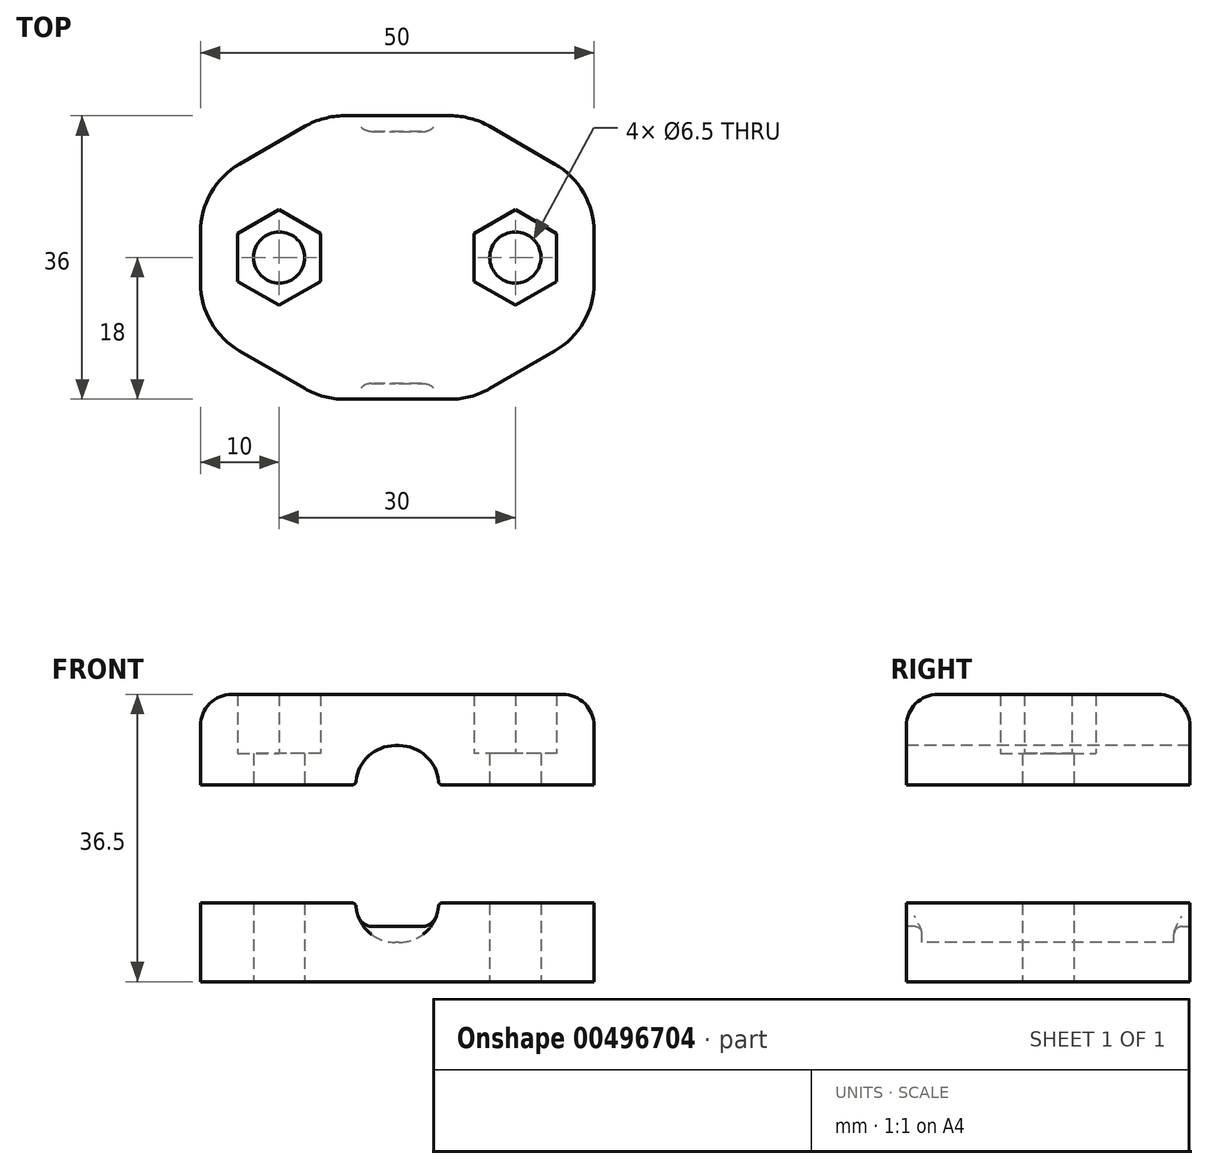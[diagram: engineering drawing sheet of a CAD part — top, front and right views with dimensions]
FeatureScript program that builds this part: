
annotation { "Feature Type Name" : "Feature", "Feature Type Description" : "" }
export const myFeature = defineFeature(function(context is Context, id is Id, definition is map)
    precondition{}
    {
        {
            var Q0;
            Q0=qCreatedBy(makeId("Top.planeOp"),FACE);
            var sketch = newSketch(context, id + "F0", { "sketchPlane" : qUnion([Q0])});
            skLineSegment(sketch, "E0.bottom", {"start": v(9.41, 18) * mm, "end": v(-9.41, 18) * mm});
            skLineSegment(sketch, "E0.top", {"start": v(9.41, -18) * mm, "end": v(-9.41, -18) * mm});
            skLineSegment(sketch, "E0.left", {"start": v(25, 9) * mm, "end": v(25, -18) * mm});
            skLineSegment(sketch, "E0.right", {"start": v(-25, 9) * mm, "end": v(-25, -9) * mm});
            skPoint(sketch, "E0.middle", {"position": v(0, 0) * mm});
            skLineSegment(sketch, "E1.0", {"start": v(9.41, 18) * mm, "end": v(25, 9) * mm});
            skLineSegment(sketch, "E1.1", {"start": v(25, 9) * mm, "end": v(25, -9) * mm});
            skLineSegment(sketch, "E1.2", {"start": v(25, -9) * mm, "end": v(9.41, -18) * mm});
            skLineSegment(sketch, "E1.3", {"start": v(-9.41, -18) * mm, "end": v(-25, -9) * mm});
            skLineSegment(sketch, "E1.4", {"start": v(-25, -9) * mm, "end": v(-25, 9) * mm});
            skLineSegment(sketch, "E1.5", {"start": v(-25, 9) * mm, "end": v(-9.41, 18) * mm});
            skPoint(sketch, "E2.orphan", {"position": v(-25, 18) * mm});
            skPoint(sketch, "E3.orphan", {"position": v(-25, -18) * mm});
            skPoint(sketch, "E4.orphan", {"position": v(25, 18) * mm});
            skSolve(sketch);
        }
        {
            var Q0;
            Q0=makeQuery(id+"F0.imprint","IMPRINT",FACE,{"disambiguationData":[TD([[makeQuery(id+"F0.imprint","IMPRINT",EDGE,{"derivedFrom":sQuery(id+"F0.wireOp",EDGE,"E0.bottom")}),1.0]])]});
            var sketch = newSketch(context, id + "F1", { "sketchPlane" : qUnion([Q0])});
            skLineSegment(sketch, "E5.bottom", {"start": v(5.25, 16) * mm, "end": v(-5.25, 16) * mm});
            skLineSegment(sketch, "E5.top", {"start": v(5.25, -16) * mm, "end": v(-5.25, -16) * mm});
            skLineSegment(sketch, "E5.left", {"start": v(5.25, 16) * mm, "end": v(5.25, -16) * mm});
            skLineSegment(sketch, "E5.right", {"start": v(-5.25, 16) * mm, "end": v(-5.25, -16) * mm});
            skPoint(sketch, "E5.middle", {"position": v(0, 0) * mm});
            skSolve(sketch);
        }
        {
            var Q0;
            Q0=qCreatedBy(makeId("Top.planeOp"),FACE);
            var sketch = newSketch(context, id + "F2", { "sketchPlane" : qUnion([Q0])});
            skLineSegment(sketch, "E6.bottom", {"start": v(5.25, 20) * mm, "end": v(-5.25, 20) * mm});
            skLineSegment(sketch, "E6.top", {"start": v(5.25, -20) * mm, "end": v(-5.25, -20) * mm});
            skLineSegment(sketch, "E6.left", {"start": v(5.25, 20) * mm, "end": v(5.25, -20) * mm});
            skLineSegment(sketch, "E6.right", {"start": v(-5.25, 20) * mm, "end": v(-5.25, -20) * mm});
            skPoint(sketch, "E6.middle", {"position": v(0, 0) * mm});
            skSolve(sketch);
        }
        {
            var Q0;
            Q0=makeQuery(id+"F0.imprint","IMPRINT",FACE,{"disambiguationData":[TD([[makeQuery(id+"F0.imprint","IMPRINT",EDGE,{"derivedFrom":sQuery(id+"F0.wireOp",EDGE,"E0.bottom")}),1.0]])]});
            var sketch = newSketch(context, id + "F3", { "sketchPlane" : qUnion([Q0])});
            skCircle(sketch, "E7", {"center": v(-15, 0) * mm, "radius": 3.25 * mm});
            skLineSegment(sketch, "E8", {"start": v(-15, 0) * mm, "end": v(15, 0) * mm, "construction": true});
            skCircle(sketch, "E9", {"center": v(15, 0) * mm, "radius": 3.25 * mm});
            skSolve(sketch);
        }
        {
            var Q0;
            Q0 = qSketchRegion(id + "F0", true);
            extrude(context, id + "F4", {"entities" : qUnion([Q0]), "depth" : 10 * mm});
        }
        {
            var Q0;
            Q0 = qSketchRegion(id + "F0", true);
            extrude(context, id + "F5", {"entities" : qUnion([Q0]), "depth" : 36.5 * mm, "hasSecondDirection" : true, "secondDirectionOppositeDirection" : false, "secondDirectionDepth" : 25 * mm, "offsetDistance" : 25 * mm});
        }
        {
            var Q0;
            Q0 = qSketchRegion(id + "F3", true);
            extrude(context, id + "F6", {"entities" : qUnion([Q0]), "operationType" : NewBodyOperationType.REMOVE, "endBound" : BoundingType.THROUGH_ALL, "depth" : 25 * mm});
        }
        {
            var Q0;
            Q0 = qSketchRegion(id + "F1", true);
            extrude(context, id + "F7", {"entities" : qUnion([Q0]), "operationType" : NewBodyOperationType.REMOVE, "depth" : 30 * mm, "hasSecondDirection" : true, "secondDirectionOppositeDirection" : false, "secondDirectionDepth" : 5 * mm});
        }
        {
            var Q0;
            Q0 = qSketchRegion(id + "F2", true);
            extrude(context, id + "F8", {"entities" : qUnion([Q0]), "operationType" : NewBodyOperationType.REMOVE, "depth" : 30 * mm, "hasSecondDirection" : true, "secondDirectionOppositeDirection" : false, "secondDirectionDepth" : 7 * mm, "offsetDistance" : 25 * mm});
        }
        {
            var Q0;
            Q0=makeQuery(id+"F3.imprint","IMPRINT",FACE,{"disambiguationData":[TD([[makeQuery(id+"F3.imprint","IMPRINT",EDGE,{"derivedFrom":sQuery(id+"F3.wireOp",EDGE,"E7")}),1.0]])]});
            var sketch = newSketch(context, id + "F9", { "sketchPlane" : qUnion([Q0])});
            skLineSegment(sketch, "E10", {"start": v(0, 0) * mm, "end": v(-15, 0) * mm});
            skLineSegment(sketch, "E11", {"start": v(-15, 0) * mm, "end": v(15, 0) * mm});
            skPoint(sketch, "E12.0.midPoint", {"position": v(-20, 0) * mm});
            skPoint(sketch, "E13.0.midPoint", {"position": v(20, 0) * mm});
            skCircle(sketch, "E14.cCircle", {"center": v(-15, 0) * mm, "radius": 5.25 * mm, "construction": true});
            skLineSegment(sketch, "E14.0", {"start": v(-20.25, -3.03) * mm, "end": v(-20.25, 3.03) * mm});
            skLineSegment(sketch, "E14.1", {"start": v(-20.25, 3.03) * mm, "end": v(-15, 6.06) * mm});
            skLineSegment(sketch, "E14.2", {"start": v(-15, 6.06) * mm, "end": v(-9.75, 3.03) * mm});
            skLineSegment(sketch, "E14.3", {"start": v(-9.75, 3.03) * mm, "end": v(-9.75, -3.03) * mm});
            skLineSegment(sketch, "E14.4", {"start": v(-9.75, -3.03) * mm, "end": v(-15, -6.06) * mm});
            skLineSegment(sketch, "E14.5", {"start": v(-15, -6.06) * mm, "end": v(-20.25, -3.03) * mm});
            skPoint(sketch, "E14.0.midPoint", {"position": v(-20.25, 0) * mm});
            skCircle(sketch, "E15.cCircle", {"center": v(15, 0) * mm, "radius": 5.25 * mm, "construction": true});
            skLineSegment(sketch, "E15.0", {"start": v(20.25, 3.03) * mm, "end": v(20.25, -3.03) * mm});
            skLineSegment(sketch, "E15.1", {"start": v(20.25, -3.03) * mm, "end": v(15, -6.06) * mm});
            skLineSegment(sketch, "E15.2", {"start": v(15, -6.06) * mm, "end": v(9.75, -3.03) * mm});
            skLineSegment(sketch, "E15.3", {"start": v(9.75, -3.03) * mm, "end": v(9.75, 3.03) * mm});
            skLineSegment(sketch, "E15.4", {"start": v(9.75, 3.03) * mm, "end": v(15, 6.06) * mm});
            skLineSegment(sketch, "E15.5", {"start": v(15, 6.06) * mm, "end": v(20.25, 3.03) * mm});
            skPoint(sketch, "E15.0.midPoint", {"position": v(20.25, 0) * mm});
            skSolve(sketch);
        }
        {
            var Q0;
            Q0 = qSketchRegion(id + "F9", true);
            extrude(context, id + "F10", {"entities" : qUnion([Q0]), "operationType" : NewBodyOperationType.REMOVE, "depth" : 40 * mm, "hasSecondDirection" : true, "secondDirectionOppositeDirection" : false, "secondDirectionDepth" : 29 * mm, "offsetDistance" : 25 * mm});
        }
        {
            var Q0;
            Q0=makeQuery(id+"F7.boolean.opBoolean","COPY",EDGE,{"derivedFrom":makeQuery(id+"F7.opExtrude","CAP_EDGE",EDGE,{"disambiguationData":[OSD([sQuery(id+"F1.wireOp",EDGE,"E5.left")])],"isStart":true})});
            var Q1;
            Q1=makeQuery(id+"F7.boolean.opBoolean","COPY",EDGE,{"derivedFrom":makeQuery(id+"F7.opExtrude","CAP_EDGE",EDGE,{"disambiguationData":[OSD([sQuery(id+"F1.wireOp",EDGE,"E5.right")])],"isStart":true})});
            var Q2;
            Q2=makeQuery(id+"F7.boolean.opBoolean","COPY",EDGE,{"derivedFrom":makeQuery(id+"F7.opExtrude","CAP_EDGE",EDGE,{"disambiguationData":[OSD([sQuery(id+"F1.wireOp",EDGE,"E5.left")])],"isStart":false})});
            var Q3;
            Q3=makeQuery(id+"F7.boolean.opBoolean","COPY",EDGE,{"derivedFrom":makeQuery(id+"F7.opExtrude","CAP_EDGE",EDGE,{"disambiguationData":[OSD([sQuery(id+"F1.wireOp",EDGE,"E5.right")])],"isStart":false})});
            fillet(context, id + "F11", {"entities" : qUnion([Q0, Q1, Q2, Q3]), "radius" : 5 * mm, "tangentPropagation" : true, "allowEdgeOverflow" : false});
        }
        {
            var Q0;
            {var subQ0=sQuery(id+"F0.wireOp",EDGE,"E0.bottom");var subQ6=sQuery(id+"F1.wireOp",EDGE,"E5.right");var subQ10=sQuery(id+"F2.wireOp",EDGE,"E6.left");var subQ12=sQuery(id+"F2.wireOp",EDGE,"E6.right");Q0=makeQuery(id+"F11.opFillet","BLEND_EDGE",EDGE,{"blendedFrom":[makeQuery(id+"F7.boolean.opBoolean","COPY",EDGE,{"derivedFrom":makeQuery(id+"F7.opExtrude","CAP_EDGE",EDGE,{"disambiguationData":[OSD([subQ6])],"isStart":true})}),makeQuery(id+"F8.boolean.opBoolean","COPY",FACE,{"disambiguationData":[TD([makeQuery(id+"F4.opExtrude","SWEPT_FACE",FACE,{"disambiguationData":[OSD([subQ0])]})])],"derivedFrom":makeQuery(id+"F8.opExtrude","CAP_FACE",FACE,{"disambiguationData":[OSD([sQuery(id+"F2.wireOp",EDGE,"E6.bottom"),sQuery(id+"F2.wireOp",EDGE,"E6.top"),subQ10,subQ12])],"isStart":true})})],"blendedInto":[makeQuery(id+"F8.boolean.opBoolean","COPY",FACE,{"disambiguationData":[TD([makeQuery(id+"F4.opExtrude","SWEPT_FACE",FACE,{"disambiguationData":[OSD([subQ0])]})])],"derivedFrom":makeQuery(id+"F8.opExtrude","CAP_FACE",FACE,{"disambiguationData":[OSD([sQuery(id+"F2.wireOp",EDGE,"E6.bottom"),sQuery(id+"F2.wireOp",EDGE,"E6.top"),subQ10,subQ12])],"isStart":true})})]});}
            var Q1;
            {var subQ0=sQuery(id+"F0.wireOp",EDGE,"E0.bottom");var subQ7=sQuery(id+"F1.wireOp",EDGE,"E5.left");var subQ10=sQuery(id+"F2.wireOp",EDGE,"E6.left");var subQ12=sQuery(id+"F2.wireOp",EDGE,"E6.right");Q1=makeQuery(id+"F11.opFillet","BLEND_EDGE",EDGE,{"blendedFrom":[makeQuery(id+"F7.boolean.opBoolean","COPY",EDGE,{"derivedFrom":makeQuery(id+"F7.opExtrude","CAP_EDGE",EDGE,{"disambiguationData":[OSD([subQ7])],"isStart":true})}),makeQuery(id+"F8.boolean.opBoolean","COPY",FACE,{"disambiguationData":[TD([makeQuery(id+"F4.opExtrude","SWEPT_FACE",FACE,{"disambiguationData":[OSD([subQ0])]})])],"derivedFrom":makeQuery(id+"F8.opExtrude","CAP_FACE",FACE,{"disambiguationData":[OSD([sQuery(id+"F2.wireOp",EDGE,"E6.bottom"),sQuery(id+"F2.wireOp",EDGE,"E6.top"),subQ10,subQ12])],"isStart":true})})],"blendedInto":[makeQuery(id+"F8.boolean.opBoolean","COPY",FACE,{"disambiguationData":[TD([makeQuery(id+"F4.opExtrude","SWEPT_FACE",FACE,{"disambiguationData":[OSD([subQ0])]})])],"derivedFrom":makeQuery(id+"F8.opExtrude","CAP_FACE",FACE,{"disambiguationData":[OSD([sQuery(id+"F2.wireOp",EDGE,"E6.bottom"),sQuery(id+"F2.wireOp",EDGE,"E6.top"),subQ10,subQ12])],"isStart":true})})]});}
            var Q2;
            {var subQ0=sQuery(id+"F0.wireOp",EDGE,"E0.top");var subQ6=sQuery(id+"F1.wireOp",EDGE,"E5.right");var subQ11=sQuery(id+"F2.wireOp",EDGE,"E6.left");var subQ12=sQuery(id+"F2.wireOp",EDGE,"E6.right");Q2=makeQuery(id+"F11.opFillet","BLEND_EDGE",EDGE,{"blendedFrom":[makeQuery(id+"F7.boolean.opBoolean","COPY",EDGE,{"derivedFrom":makeQuery(id+"F7.opExtrude","CAP_EDGE",EDGE,{"disambiguationData":[OSD([subQ6])],"isStart":true})}),makeQuery(id+"F8.boolean.opBoolean","COPY",FACE,{"disambiguationData":[TD([makeQuery(id+"F4.opExtrude","SWEPT_FACE",FACE,{"disambiguationData":[OSD([subQ0])]})])],"derivedFrom":makeQuery(id+"F8.opExtrude","CAP_FACE",FACE,{"disambiguationData":[OSD([sQuery(id+"F2.wireOp",EDGE,"E6.bottom"),sQuery(id+"F2.wireOp",EDGE,"E6.top"),subQ11,subQ12])],"isStart":true})})],"blendedInto":[makeQuery(id+"F8.boolean.opBoolean","COPY",FACE,{"disambiguationData":[TD([makeQuery(id+"F4.opExtrude","SWEPT_FACE",FACE,{"disambiguationData":[OSD([subQ0])]})])],"derivedFrom":makeQuery(id+"F8.opExtrude","CAP_FACE",FACE,{"disambiguationData":[OSD([sQuery(id+"F2.wireOp",EDGE,"E6.bottom"),sQuery(id+"F2.wireOp",EDGE,"E6.top"),subQ11,subQ12])],"isStart":true})})]});}
            var Q3;
            {var subQ0=sQuery(id+"F0.wireOp",EDGE,"E0.top");var subQ7=sQuery(id+"F1.wireOp",EDGE,"E5.left");var subQ11=sQuery(id+"F2.wireOp",EDGE,"E6.left");var subQ12=sQuery(id+"F2.wireOp",EDGE,"E6.right");Q3=makeQuery(id+"F11.opFillet","BLEND_EDGE",EDGE,{"blendedFrom":[makeQuery(id+"F7.boolean.opBoolean","COPY",EDGE,{"derivedFrom":makeQuery(id+"F7.opExtrude","CAP_EDGE",EDGE,{"disambiguationData":[OSD([subQ7])],"isStart":true})}),makeQuery(id+"F8.boolean.opBoolean","COPY",FACE,{"disambiguationData":[TD([makeQuery(id+"F4.opExtrude","SWEPT_FACE",FACE,{"disambiguationData":[OSD([subQ0])]})])],"derivedFrom":makeQuery(id+"F8.opExtrude","CAP_FACE",FACE,{"disambiguationData":[OSD([sQuery(id+"F2.wireOp",EDGE,"E6.bottom"),sQuery(id+"F2.wireOp",EDGE,"E6.top"),subQ11,subQ12])],"isStart":true})})],"blendedInto":[makeQuery(id+"F8.boolean.opBoolean","COPY",FACE,{"disambiguationData":[TD([makeQuery(id+"F4.opExtrude","SWEPT_FACE",FACE,{"disambiguationData":[OSD([subQ0])]})])],"derivedFrom":makeQuery(id+"F8.opExtrude","CAP_FACE",FACE,{"disambiguationData":[OSD([sQuery(id+"F2.wireOp",EDGE,"E6.bottom"),sQuery(id+"F2.wireOp",EDGE,"E6.top"),subQ11,subQ12])],"isStart":true})})]});}
            var Q4;
            {var subQ0=sQuery(id+"F0.wireOp",EDGE,"E0.bottom");var subQ6=sQuery(id+"F1.wireOp",EDGE,"E5.right");var subQ10=sQuery(id+"F2.wireOp",EDGE,"E6.right");var subQ12=sQuery(id+"F2.wireOp",EDGE,"E6.left");Q4=makeQuery(id+"F11.opFillet","BLEND_EDGE",EDGE,{"blendedFrom":[makeQuery(id+"F7.boolean.opBoolean","COPY",EDGE,{"derivedFrom":makeQuery(id+"F7.opExtrude","CAP_EDGE",EDGE,{"disambiguationData":[OSD([subQ6])],"isStart":false})}),makeQuery(id+"F8.boolean.opBoolean","COPY",FACE,{"disambiguationData":[TD([makeQuery(id+"F5.opExtrude","SWEPT_FACE",FACE,{"disambiguationData":[OSD([subQ0])]})])],"derivedFrom":makeQuery(id+"F8.opExtrude","CAP_FACE",FACE,{"disambiguationData":[OSD([sQuery(id+"F2.wireOp",EDGE,"E6.bottom"),sQuery(id+"F2.wireOp",EDGE,"E6.top"),subQ12,subQ10])],"isStart":false})})],"blendedInto":[makeQuery(id+"F8.boolean.opBoolean","COPY",FACE,{"disambiguationData":[TD([makeQuery(id+"F5.opExtrude","SWEPT_FACE",FACE,{"disambiguationData":[OSD([subQ0])]})])],"derivedFrom":makeQuery(id+"F8.opExtrude","CAP_FACE",FACE,{"disambiguationData":[OSD([sQuery(id+"F2.wireOp",EDGE,"E6.bottom"),sQuery(id+"F2.wireOp",EDGE,"E6.top"),subQ12,subQ10])],"isStart":false})})]});}
            var Q5;
            {var subQ0=sQuery(id+"F0.wireOp",EDGE,"E0.bottom");var subQ7=sQuery(id+"F1.wireOp",EDGE,"E5.left");var subQ10=sQuery(id+"F2.wireOp",EDGE,"E6.right");var subQ12=sQuery(id+"F2.wireOp",EDGE,"E6.left");Q5=makeQuery(id+"F11.opFillet","BLEND_EDGE",EDGE,{"blendedFrom":[makeQuery(id+"F7.boolean.opBoolean","COPY",EDGE,{"derivedFrom":makeQuery(id+"F7.opExtrude","CAP_EDGE",EDGE,{"disambiguationData":[OSD([subQ7])],"isStart":false})}),makeQuery(id+"F8.boolean.opBoolean","COPY",FACE,{"disambiguationData":[TD([makeQuery(id+"F5.opExtrude","SWEPT_FACE",FACE,{"disambiguationData":[OSD([subQ0])]})])],"derivedFrom":makeQuery(id+"F8.opExtrude","CAP_FACE",FACE,{"disambiguationData":[OSD([sQuery(id+"F2.wireOp",EDGE,"E6.bottom"),sQuery(id+"F2.wireOp",EDGE,"E6.top"),subQ12,subQ10])],"isStart":false})})],"blendedInto":[makeQuery(id+"F8.boolean.opBoolean","COPY",FACE,{"disambiguationData":[TD([makeQuery(id+"F5.opExtrude","SWEPT_FACE",FACE,{"disambiguationData":[OSD([subQ0])]})])],"derivedFrom":makeQuery(id+"F8.opExtrude","CAP_FACE",FACE,{"disambiguationData":[OSD([sQuery(id+"F2.wireOp",EDGE,"E6.bottom"),sQuery(id+"F2.wireOp",EDGE,"E6.top"),subQ12,subQ10])],"isStart":false})})]});}
            var Q6;
            {var subQ0=sQuery(id+"F0.wireOp",EDGE,"E0.top");var subQ7=sQuery(id+"F1.wireOp",EDGE,"E5.left");var subQ11=sQuery(id+"F2.wireOp",EDGE,"E6.right");var subQ12=sQuery(id+"F2.wireOp",EDGE,"E6.left");Q6=makeQuery(id+"F11.opFillet","BLEND_EDGE",EDGE,{"blendedFrom":[makeQuery(id+"F7.boolean.opBoolean","COPY",EDGE,{"derivedFrom":makeQuery(id+"F7.opExtrude","CAP_EDGE",EDGE,{"disambiguationData":[OSD([subQ7])],"isStart":false})}),makeQuery(id+"F8.boolean.opBoolean","COPY",FACE,{"disambiguationData":[TD([makeQuery(id+"F5.opExtrude","SWEPT_FACE",FACE,{"disambiguationData":[OSD([subQ0])]})])],"derivedFrom":makeQuery(id+"F8.opExtrude","CAP_FACE",FACE,{"disambiguationData":[OSD([sQuery(id+"F2.wireOp",EDGE,"E6.bottom"),sQuery(id+"F2.wireOp",EDGE,"E6.top"),subQ12,subQ11])],"isStart":false})})],"blendedInto":[makeQuery(id+"F8.boolean.opBoolean","COPY",FACE,{"disambiguationData":[TD([makeQuery(id+"F5.opExtrude","SWEPT_FACE",FACE,{"disambiguationData":[OSD([subQ0])]})])],"derivedFrom":makeQuery(id+"F8.opExtrude","CAP_FACE",FACE,{"disambiguationData":[OSD([sQuery(id+"F2.wireOp",EDGE,"E6.bottom"),sQuery(id+"F2.wireOp",EDGE,"E6.top"),subQ12,subQ11])],"isStart":false})})]});}
            var Q7;
            {var subQ0=sQuery(id+"F0.wireOp",EDGE,"E0.top");var subQ6=sQuery(id+"F1.wireOp",EDGE,"E5.right");var subQ11=sQuery(id+"F2.wireOp",EDGE,"E6.right");var subQ12=sQuery(id+"F2.wireOp",EDGE,"E6.left");Q7=makeQuery(id+"F11.opFillet","BLEND_EDGE",EDGE,{"blendedFrom":[makeQuery(id+"F7.boolean.opBoolean","COPY",EDGE,{"derivedFrom":makeQuery(id+"F7.opExtrude","CAP_EDGE",EDGE,{"disambiguationData":[OSD([subQ6])],"isStart":false})}),makeQuery(id+"F8.boolean.opBoolean","COPY",FACE,{"disambiguationData":[TD([makeQuery(id+"F5.opExtrude","SWEPT_FACE",FACE,{"disambiguationData":[OSD([subQ0])]})])],"derivedFrom":makeQuery(id+"F8.opExtrude","CAP_FACE",FACE,{"disambiguationData":[OSD([sQuery(id+"F2.wireOp",EDGE,"E6.bottom"),sQuery(id+"F2.wireOp",EDGE,"E6.top"),subQ12,subQ11])],"isStart":false})})],"blendedInto":[makeQuery(id+"F8.boolean.opBoolean","COPY",FACE,{"disambiguationData":[TD([makeQuery(id+"F5.opExtrude","SWEPT_FACE",FACE,{"disambiguationData":[OSD([subQ0])]})])],"derivedFrom":makeQuery(id+"F8.opExtrude","CAP_FACE",FACE,{"disambiguationData":[OSD([sQuery(id+"F2.wireOp",EDGE,"E6.bottom"),sQuery(id+"F2.wireOp",EDGE,"E6.top"),subQ12,subQ11])],"isStart":false})})]});}
            fillet(context, id + "F12", {"entities" : qUnion([Q0, Q1, Q2, Q3, Q4, Q5, Q6, Q7]), "radius" : 2 * mm, "allowEdgeOverflow" : false});
        }
        {
            var Q0;
            {var subQ0=sQuery(id+"F1.wireOp",EDGE,"E5.right");var subQ1=sQuery(id+"F1.wireOp",EDGE,"E5.left");var subQ2=sQuery(id+"F1.wireOp",EDGE,"E5.bottom");Q0=makeQuery(id+"F8.boolean.opBoolean","INTERSECT",EDGE,{"derivedFrom":[makeQuery(id+"F7.boolean.opBoolean","COPY",FACE,{"disambiguationData":[TD([makeQuery(id+"F7.opExtrude","CAP_FACE",FACE,{"disambiguationData":[OSD([subQ2,sQuery(id+"F1.wireOp",EDGE,"E5.top"),subQ1,subQ0])],"isStart":true})])],"derivedFrom":makeQuery(id+"F7.opExtrude","SWEPT_FACE",FACE,{"disambiguationData":[OSD([subQ2])]})}),makeQuery(id+"F8.opExtrude","CAP_FACE",FACE,{"disambiguationData":[OSD([sQuery(id+"F2.wireOp",EDGE,"E6.bottom"),sQuery(id+"F2.wireOp",EDGE,"E6.top"),sQuery(id+"F2.wireOp",EDGE,"E6.left"),sQuery(id+"F2.wireOp",EDGE,"E6.right")])],"isStart":true})]});}
            var Q1;
            {var subQ0=sQuery(id+"F1.wireOp",EDGE,"E5.right");var subQ1=sQuery(id+"F1.wireOp",EDGE,"E5.left");var subQ2=sQuery(id+"F1.wireOp",EDGE,"E5.top");Q1=makeQuery(id+"F8.boolean.opBoolean","INTERSECT",EDGE,{"derivedFrom":[makeQuery(id+"F7.boolean.opBoolean","COPY",FACE,{"disambiguationData":[TD([makeQuery(id+"F7.opExtrude","CAP_FACE",FACE,{"disambiguationData":[OSD([sQuery(id+"F1.wireOp",EDGE,"E5.bottom"),subQ2,subQ1,subQ0])],"isStart":true})])],"derivedFrom":makeQuery(id+"F7.opExtrude","SWEPT_FACE",FACE,{"disambiguationData":[OSD([subQ2])]})}),makeQuery(id+"F8.opExtrude","CAP_FACE",FACE,{"disambiguationData":[OSD([sQuery(id+"F2.wireOp",EDGE,"E6.bottom"),sQuery(id+"F2.wireOp",EDGE,"E6.top"),sQuery(id+"F2.wireOp",EDGE,"E6.left"),sQuery(id+"F2.wireOp",EDGE,"E6.right")])],"isStart":true})]});}
            fillet(context, id + "F13", {"entities" : qUnion([Q0, Q1]), "radius" : 1 * mm, "tangentPropagation" : true, "allowEdgeOverflow" : false});
        }
        {
            var Q0;
            {var subQ0=sQuery(id+"F0.wireOp",EDGE,"E1.0");var subQ1=sQuery(id+"F0.wireOp",EDGE,"E0.top");var subQ2=sQuery(id+"F0.wireOp",EDGE,"E1.1");var subQ3=sQuery(id+"F0.wireOp",EDGE,"E0.bottom");var subQ4=sQuery(id+"F0.wireOp",EDGE,"E1.2");var subQ5=sQuery(id+"F0.wireOp",EDGE,"E1.5");var subQ6=sQuery(id+"F0.wireOp",EDGE,"E1.4");var subQ7=sQuery(id+"F0.wireOp",EDGE,"E1.3");var subQ8=makeQuery(id+"F4.opExtrude","CAP_FACE",FACE,{"disambiguationData":[OSD([subQ3,subQ1,subQ0,subQ2,subQ4,subQ7,subQ6,subQ5])],"isStart":false});var subQ11=sQuery(id+"F1.wireOp",EDGE,"E5.left");Q0=makeQuery(id+"F11.opFillet","BLEND_EDGE",EDGE,{"blendedFrom":[makeQuery(id+"F7.boolean.opBoolean","COPY",EDGE,{"derivedFrom":makeQuery(id+"F7.opExtrude","CAP_EDGE",EDGE,{"disambiguationData":[OSD([subQ11])],"isStart":true})}),makeQuery(id+"F8.boolean.opBoolean","SPLIT",FACE,{"disambiguationData":[TD([makeQuery(id+"F4.opExtrude","SWEPT_FACE",FACE,{"disambiguationData":[OSD([subQ0])]})])],"derivedFrom":subQ8})],"blendedInto":[makeQuery(id+"F8.boolean.opBoolean","SPLIT",FACE,{"disambiguationData":[TD([makeQuery(id+"F4.opExtrude","SWEPT_FACE",FACE,{"disambiguationData":[OSD([subQ0])]})])],"derivedFrom":subQ8})]});}
            var Q1;
            {var subQ0=sQuery(id+"F0.wireOp",EDGE,"E1.0");var subQ1=sQuery(id+"F0.wireOp",EDGE,"E1.5");var subQ2=sQuery(id+"F0.wireOp",EDGE,"E1.4");var subQ3=sQuery(id+"F0.wireOp",EDGE,"E1.3");var subQ4=sQuery(id+"F0.wireOp",EDGE,"E1.2");var subQ5=sQuery(id+"F0.wireOp",EDGE,"E1.1");var subQ6=sQuery(id+"F0.wireOp",EDGE,"E0.top");var subQ7=sQuery(id+"F0.wireOp",EDGE,"E0.bottom");var subQ8=makeQuery(id+"F5.opExtrude","CAP_FACE",FACE,{"disambiguationData":[OSD([subQ7,subQ6,subQ0,subQ5,subQ4,subQ3,subQ2,subQ1])],"isStart":true});var subQ11=sQuery(id+"F1.wireOp",EDGE,"E5.left");Q1=makeQuery(id+"F11.opFillet","BLEND_EDGE",EDGE,{"blendedFrom":[makeQuery(id+"F7.boolean.opBoolean","COPY",EDGE,{"derivedFrom":makeQuery(id+"F7.opExtrude","CAP_EDGE",EDGE,{"disambiguationData":[OSD([subQ11])],"isStart":false})}),makeQuery(id+"F8.boolean.opBoolean","SPLIT",FACE,{"disambiguationData":[TD([makeQuery(id+"F5.opExtrude","SWEPT_FACE",FACE,{"disambiguationData":[OSD([subQ0])]})])],"derivedFrom":subQ8})],"blendedInto":[makeQuery(id+"F8.boolean.opBoolean","SPLIT",FACE,{"disambiguationData":[TD([makeQuery(id+"F5.opExtrude","SWEPT_FACE",FACE,{"disambiguationData":[OSD([subQ0])]})])],"derivedFrom":subQ8})]});}
            var Q2;
            {var subQ0=sQuery(id+"F0.wireOp",EDGE,"E1.3");var subQ1=sQuery(id+"F0.wireOp",EDGE,"E1.4");var subQ2=sQuery(id+"F0.wireOp",EDGE,"E0.top");var subQ3=sQuery(id+"F0.wireOp",EDGE,"E0.bottom");var subQ4=sQuery(id+"F0.wireOp",EDGE,"E1.5");var subQ5=sQuery(id+"F0.wireOp",EDGE,"E1.2");var subQ6=sQuery(id+"F0.wireOp",EDGE,"E1.1");var subQ7=sQuery(id+"F0.wireOp",EDGE,"E1.0");var subQ8=makeQuery(id+"F5.opExtrude","CAP_FACE",FACE,{"disambiguationData":[OSD([subQ3,subQ2,subQ7,subQ6,subQ5,subQ0,subQ1,subQ4])],"isStart":true});var subQ11=sQuery(id+"F1.wireOp",EDGE,"E5.right");Q2=makeQuery(id+"F11.opFillet","BLEND_EDGE",EDGE,{"blendedFrom":[makeQuery(id+"F7.boolean.opBoolean","COPY",EDGE,{"derivedFrom":makeQuery(id+"F7.opExtrude","CAP_EDGE",EDGE,{"disambiguationData":[OSD([subQ11])],"isStart":false})}),makeQuery(id+"F8.boolean.opBoolean","SPLIT",FACE,{"disambiguationData":[TD([makeQuery(id+"F5.opExtrude","SWEPT_FACE",FACE,{"disambiguationData":[OSD([subQ0])]})])],"derivedFrom":subQ8})],"blendedInto":[makeQuery(id+"F8.boolean.opBoolean","SPLIT",FACE,{"disambiguationData":[TD([makeQuery(id+"F5.opExtrude","SWEPT_FACE",FACE,{"disambiguationData":[OSD([subQ0])]})])],"derivedFrom":subQ8})]});}
            var Q3;
            {var subQ0=sQuery(id+"F0.wireOp",EDGE,"E1.3");var subQ1=sQuery(id+"F0.wireOp",EDGE,"E1.4");var subQ2=sQuery(id+"F0.wireOp",EDGE,"E1.5");var subQ3=sQuery(id+"F0.wireOp",EDGE,"E1.2");var subQ4=sQuery(id+"F0.wireOp",EDGE,"E1.1");var subQ5=sQuery(id+"F0.wireOp",EDGE,"E1.0");var subQ6=sQuery(id+"F0.wireOp",EDGE,"E0.top");var subQ7=sQuery(id+"F0.wireOp",EDGE,"E0.bottom");var subQ8=makeQuery(id+"F4.opExtrude","CAP_FACE",FACE,{"disambiguationData":[OSD([subQ7,subQ6,subQ5,subQ4,subQ3,subQ0,subQ1,subQ2])],"isStart":false});var subQ11=sQuery(id+"F1.wireOp",EDGE,"E5.right");Q3=makeQuery(id+"F11.opFillet","BLEND_EDGE",EDGE,{"blendedFrom":[makeQuery(id+"F7.boolean.opBoolean","COPY",EDGE,{"derivedFrom":makeQuery(id+"F7.opExtrude","CAP_EDGE",EDGE,{"disambiguationData":[OSD([subQ11])],"isStart":true})}),makeQuery(id+"F8.boolean.opBoolean","SPLIT",FACE,{"disambiguationData":[TD([makeQuery(id+"F4.opExtrude","SWEPT_FACE",FACE,{"disambiguationData":[OSD([subQ0])]})])],"derivedFrom":subQ8})],"blendedInto":[makeQuery(id+"F8.boolean.opBoolean","SPLIT",FACE,{"disambiguationData":[TD([makeQuery(id+"F4.opExtrude","SWEPT_FACE",FACE,{"disambiguationData":[OSD([subQ0])]})])],"derivedFrom":subQ8})]});}
            fillet(context, id + "F14", {"entities" : qUnion([Q0, Q1, Q2, Q3]), "radius" : .5 * mm, "allowEdgeOverflow" : false});
        }
        {
            var Q0;
            Q0=makeQuery(id+"F5.opExtrude","SWEPT_EDGE",EDGE,{"disambiguationData":[OSD([sQuery(id+"F0.wireOp",EDGE,"E0.top"),sQuery(id+"F0.wireOp",EDGE,"E1.3")])]});
            var Q1;
            Q1=makeQuery(id+"F5.opExtrude","SWEPT_EDGE",EDGE,{"disambiguationData":[OSD([sQuery(id+"F0.wireOp",EDGE,"E0.top"),sQuery(id+"F0.wireOp",EDGE,"E1.2")])]});
            var Q2;
            Q2=makeQuery(id+"F5.opExtrude","SWEPT_EDGE",EDGE,{"disambiguationData":[OSD([sQuery(id+"F0.wireOp",EDGE,"E1.1"),sQuery(id+"F0.wireOp",EDGE,"E1.2")])]});
            var Q3;
            Q3=makeQuery(id+"F5.opExtrude","SWEPT_EDGE",EDGE,{"disambiguationData":[OSD([sQuery(id+"F0.wireOp",EDGE,"E1.0"),sQuery(id+"F0.wireOp",EDGE,"E1.1")])]});
            var Q4;
            Q4=makeQuery(id+"F5.opExtrude","SWEPT_EDGE",EDGE,{"disambiguationData":[OSD([sQuery(id+"F0.wireOp",EDGE,"E0.bottom"),sQuery(id+"F0.wireOp",EDGE,"E1.0")])]});
            var Q5;
            Q5=makeQuery(id+"F5.opExtrude","SWEPT_EDGE",EDGE,{"disambiguationData":[OSD([sQuery(id+"F0.wireOp",EDGE,"E0.bottom"),sQuery(id+"F0.wireOp",EDGE,"E1.5")])]});
            var Q6;
            Q6=makeQuery(id+"F5.opExtrude","SWEPT_EDGE",EDGE,{"disambiguationData":[OSD([sQuery(id+"F0.wireOp",EDGE,"E1.4"),sQuery(id+"F0.wireOp",EDGE,"E1.5")])]});
            var Q7;
            Q7=makeQuery(id+"F5.opExtrude","SWEPT_EDGE",EDGE,{"disambiguationData":[OSD([sQuery(id+"F0.wireOp",EDGE,"E1.3"),sQuery(id+"F0.wireOp",EDGE,"E1.4")])]});
            var Q8;
            Q8=makeQuery(id+"F4.opExtrude","SWEPT_EDGE",EDGE,{"disambiguationData":[OSD([sQuery(id+"F0.wireOp",EDGE,"E1.3"),sQuery(id+"F0.wireOp",EDGE,"E1.4")])]});
            var Q9;
            Q9=makeQuery(id+"F4.opExtrude","SWEPT_EDGE",EDGE,{"disambiguationData":[OSD([sQuery(id+"F0.wireOp",EDGE,"E0.top"),sQuery(id+"F0.wireOp",EDGE,"E1.3")])]});
            var Q10;
            Q10=makeQuery(id+"F4.opExtrude","SWEPT_EDGE",EDGE,{"disambiguationData":[OSD([sQuery(id+"F0.wireOp",EDGE,"E1.4"),sQuery(id+"F0.wireOp",EDGE,"E1.5")])]});
            var Q11;
            Q11=makeQuery(id+"F4.opExtrude","SWEPT_EDGE",EDGE,{"disambiguationData":[OSD([sQuery(id+"F0.wireOp",EDGE,"E0.bottom"),sQuery(id+"F0.wireOp",EDGE,"E1.5")])]});
            var Q12;
            Q12=makeQuery(id+"F4.opExtrude","SWEPT_EDGE",EDGE,{"disambiguationData":[OSD([sQuery(id+"F0.wireOp",EDGE,"E0.bottom"),sQuery(id+"F0.wireOp",EDGE,"E1.0")])]});
            var Q13;
            Q13=makeQuery(id+"F4.opExtrude","SWEPT_EDGE",EDGE,{"disambiguationData":[OSD([sQuery(id+"F0.wireOp",EDGE,"E1.0"),sQuery(id+"F0.wireOp",EDGE,"E1.1")])]});
            var Q14;
            Q14=makeQuery(id+"F4.opExtrude","SWEPT_EDGE",EDGE,{"disambiguationData":[OSD([sQuery(id+"F0.wireOp",EDGE,"E1.1"),sQuery(id+"F0.wireOp",EDGE,"E1.2")])]});
            var Q15;
            Q15=makeQuery(id+"F4.opExtrude","SWEPT_EDGE",EDGE,{"disambiguationData":[OSD([sQuery(id+"F0.wireOp",EDGE,"E0.top"),sQuery(id+"F0.wireOp",EDGE,"E1.2")])]});
            fillet(context, id + "F15", {"entities" : qUnion([Q0, Q1, Q2, Q3, Q4, Q5, Q6, Q7, Q8, Q9, Q10, Q11, Q12, Q13, Q14, Q15]), "radius" : 10 * mm, "tangentPropagation" : true, "allowEdgeOverflow" : false});
        }
        {
            var Q0;
            Q0=makeQuery(id+"F5.opExtrude","CAP_EDGE",EDGE,{"disambiguationData":[OSD([sQuery(id+"F0.wireOp",EDGE,"E1.0")])],"isStart":false});
            fillet(context, id + "F16", {"entities" : qUnion([Q0]), "radius" : 4 * mm, "tangentPropagation" : true, "allowEdgeOverflow" : false});
        }
    });
